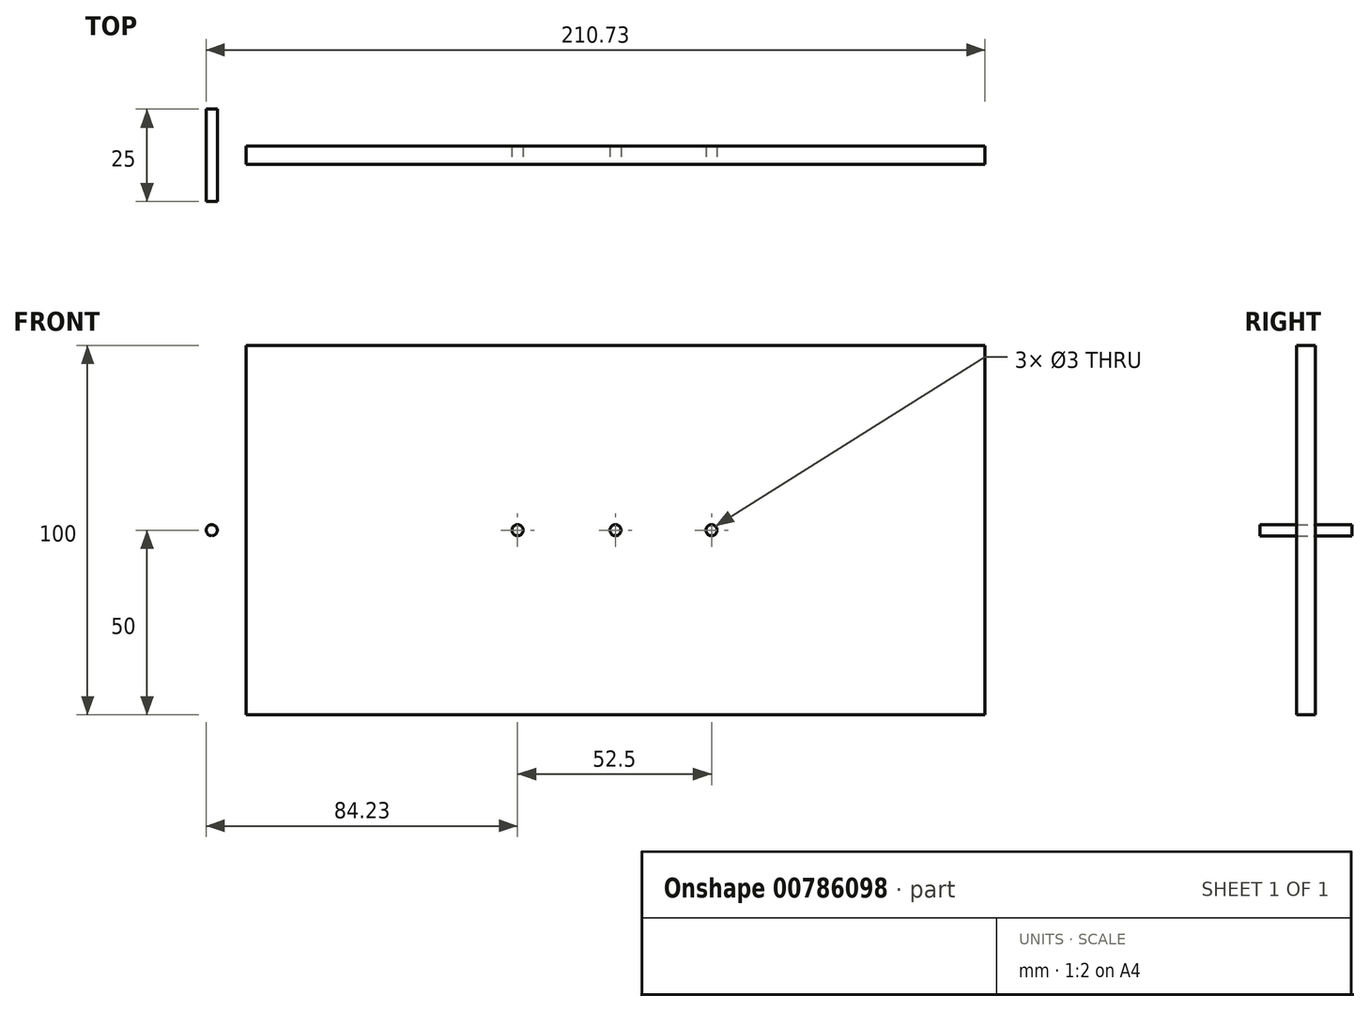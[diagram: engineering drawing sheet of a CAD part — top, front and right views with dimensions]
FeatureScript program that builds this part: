
annotation { "Feature Type Name" : "Feature", "Feature Type Description" : "" }
export const myFeature = defineFeature(function(context is Context, id is Id, definition is map)
    precondition{}
    {
        {
            var Q0;
            Q0=qCreatedBy(makeId("Front.planeOp"),FACE);
            var sketch = newSketch(context, id + "F0", { "sketchPlane" : qUnion([Q0])});
            skLineSegment(sketch, "E0.bottom", {"start": v(-100, 50) * mm, "end": v(100, 50) * mm});
            skLineSegment(sketch, "E0.top", {"start": v(-100, -50) * mm, "end": v(100, -50) * mm});
            skLineSegment(sketch, "E0.left", {"start": v(-100, 50) * mm, "end": v(-100, -50) * mm});
            skLineSegment(sketch, "E0.right", {"start": v(100, 50) * mm, "end": v(100, -50) * mm});
            skPoint(sketch, "E0.middle", {"position": v(0, 0) * mm});
            skSolve(sketch);
        }
        {
            var Q0;
            Q0 = qSketchRegion(id + "F0", true);
            extrude(context, id + "F1", {"entities" : qUnion([Q0]), "endBound" : BoundingType.SYMMETRIC, "depth" : 5 * mm, "offsetDistance" : 25 * mm});
        }
        {
            var Q0;
            Q0=makeQuery(id+"F1.opExtrude","CAP_FACE",FACE,{"disambiguationData":[OSD([sQuery(id+"F0.wireOp",EDGE,"E0.bottom"),sQuery(id+"F0.wireOp",EDGE,"E0.top"),sQuery(id+"F0.wireOp",EDGE,"E0.left"),sQuery(id+"F0.wireOp",EDGE,"E0.right")])],"isStart":false});
            var sketch = newSketch(context, id + "F2", { "sketchPlane" : qUnion([Q0])});
            skCircle(sketch, "E1", {"center": v(-26.5, 0) * mm, "radius": 1.5 * mm});
            skCircle(sketch, "E2", {"center": v(0, 0) * mm, "radius": 1.5 * mm});
            skCircle(sketch, "E3", {"center": v(26, 0) * mm, "radius": 1.5 * mm});
            skSolve(sketch);
        }
        {
            var Q0;
            Q0 = qSketchRegion(id + "F2", true);
            extrude(context, id + "F3", {"entities" : qUnion([Q0]), "operationType" : NewBodyOperationType.REMOVE, "oppositeDirection" : true, "depth" : 25 * mm, "offsetDistance" : 25 * mm});
        }
        {
            var Q0;
            Q0=qCreatedBy(makeId("Front.planeOp"),FACE);
            var sketch = newSketch(context, id + "F4", { "sketchPlane" : qUnion([Q0])});
            skCircle(sketch, "E4", {"center": v(-109.23, 0) * mm, "radius": 1.5 * mm});
            skSolve(sketch);
        }
        {
            var Q0;
            Q0 = qSketchRegion(id + "F4", true);
            extrude(context, id + "F5", {"entities" : qUnion([Q0]), "endBound" : BoundingType.SYMMETRIC, "depth" : 25 * mm, "offsetDistance" : 25 * mm});
        }
    });
